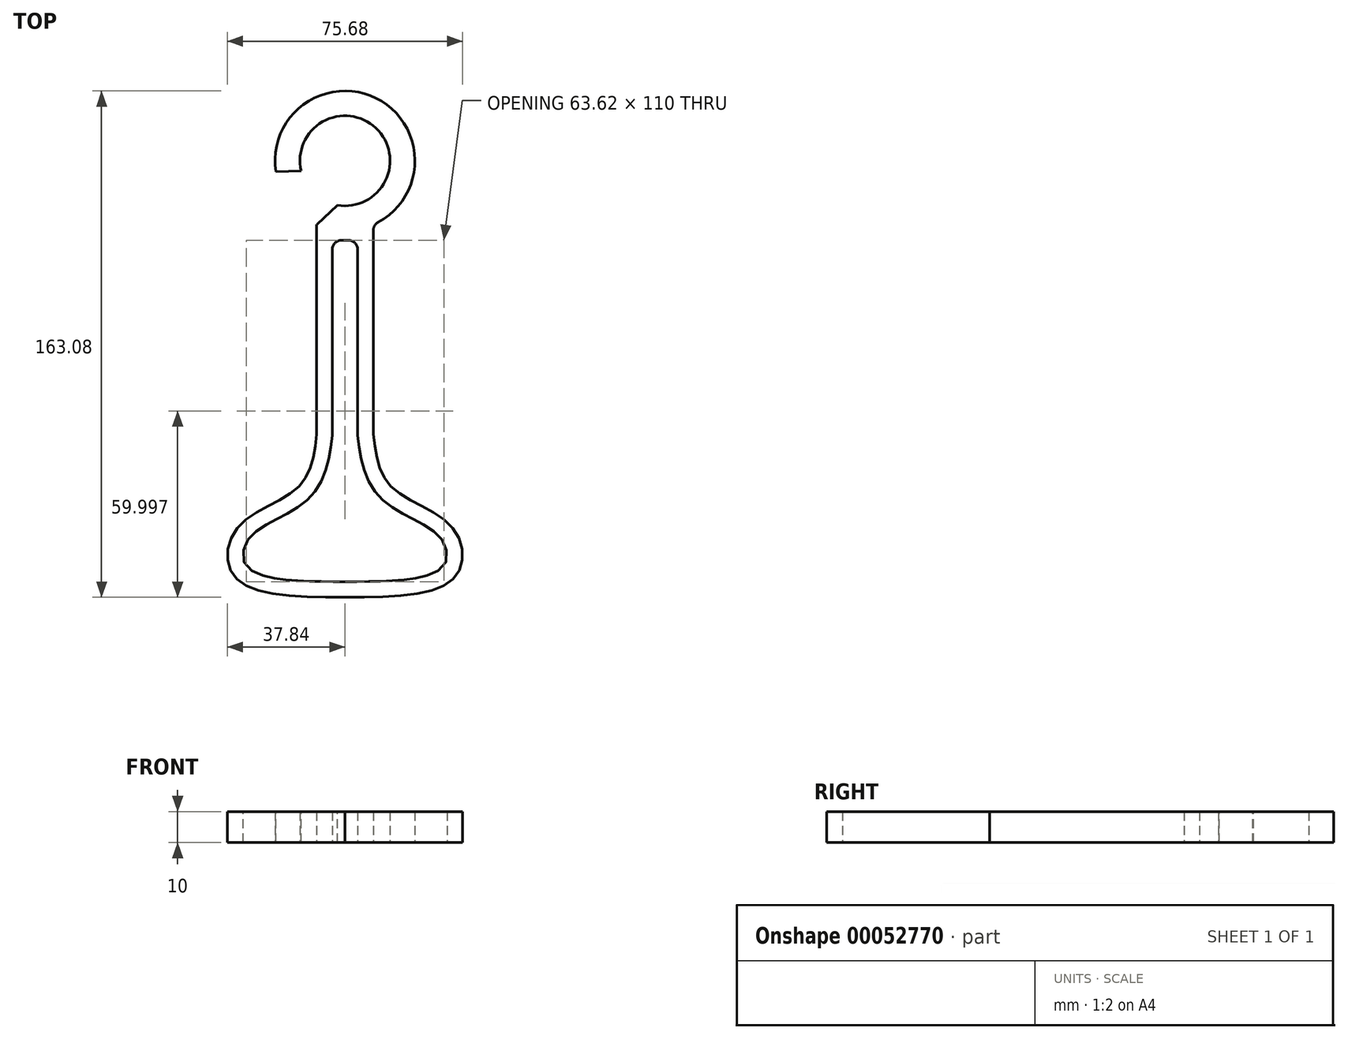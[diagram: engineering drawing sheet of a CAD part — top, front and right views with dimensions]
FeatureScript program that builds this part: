
annotation { "Feature Type Name" : "Feature", "Feature Type Description" : "" }
export const myFeature = defineFeature(function(context is Context, id is Id, definition is map)
    precondition{}
    {
        {
            var Q0;
            Q0=qCreatedBy(makeId("Top.planeOp"),FACE);
            var sketch = newSketch(context, id + "F0", { "sketchPlane" : qUnion([Q0])});
            skLineSegment(sketch, "E0", {"start": v(0, 67.57) * mm, "end": v(9.1, 67.57) * mm});
            skLineSegment(sketch, "E1", {"start": v(9.1, 67.57) * mm, "end": v(9.1, 0) * mm});
            skFitSpline(sketch, "E2", {"points": [v(9.1, 0) * mm, v(15.06, -16.95) * mm, v(34.56, -29.95) * mm, v(35.37, -45.93) * mm, v(0, -52.43) * mm], "startDerivative": vector(10.58, -85.23) * mm, "endDerivative": vector(-142.58, -0.73) * mm});
            skLineSegment(sketch, "E3", {"start": v(0, 67.57) * mm, "end": v(0, -52.43) * mm});
            skSolve(sketch);
        }
        {
            var Q0;
            Q0 = qSketchRegion(id + "F0", true);
            extrude(context, id + "F1", {"entities" : qUnion([Q0]), "depth" : 10 * mm});
        }
        {
            var Q0;
            Q0=makeQuery(id+"F1.opExtrude","SWEPT_BODY",BODY,{"disambiguationData":[OSD([sQuery(id+"F0.wireOp",EDGE,"E0"),sQuery(id+"F0.wireOp",EDGE,"E1"),sQuery(id+"F0.wireOp",EDGE,"E2"),sQuery(id+"F0.wireOp",EDGE,"E3")])]});
            var Q1;
            Q1=qCreatedBy(makeId("Right.planeOp"),FACE);
            mirror(context, id + "F2", {"operationType" : NewBodyOperationType.ADD, "entities" : qUnion([Q0]), "mirrorPlane" : qUnion([Q1])});
        }
        {
            var Q0;
            {var subQ0=makeQuery(id+"F1.opExtrude","CAP_FACE",FACE,{"disambiguationData":[OSD([sQuery(id+"F0.wireOp",EDGE,"E0"),sQuery(id+"F0.wireOp",EDGE,"E1"),sQuery(id+"F0.wireOp",EDGE,"E2"),sQuery(id+"F0.wireOp",EDGE,"E3")])],"isStart":false});Q0=makeQuery(id+"F2.boolean.opBoolean","MERGE",FACE,{"derivedFrom":[subQ0,makeQuery(id+"F2.opPattern","COPY",FACE,{"derivedFrom":subQ0,"instanceName":"1"})]});}
            var Q1;
            {var subQ0=makeQuery(id+"F1.opExtrude","CAP_FACE",FACE,{"disambiguationData":[OSD([sQuery(id+"F0.wireOp",EDGE,"E0"),sQuery(id+"F0.wireOp",EDGE,"E1"),sQuery(id+"F0.wireOp",EDGE,"E2"),sQuery(id+"F0.wireOp",EDGE,"E3")])],"isStart":true});Q1=makeQuery(id+"F2.boolean.opBoolean","MERGE",FACE,{"derivedFrom":[subQ0,makeQuery(id+"F2.opPattern","COPY",FACE,{"derivedFrom":subQ0,"instanceName":"1"})]});}
            shell(context, id + "F3", {"entities" : qUnion([Q0, Q1]), "thickness" : 5 * mm});
        }
        {
            var Q0;
            Q0=qCreatedBy(makeId("Top.planeOp"),FACE);
            var sketch = newSketch(context, id + "F4", { "sketchPlane" : qUnion([Q0])});
            skCircle(sketch, "E4", {"center": v(0, 88.15) * mm, "radius": 22.5 * mm});
            skSolve(sketch);
        }
        {
            var Q0;
            Q0=makeQuery(id+"F4.imprint","IMPRINT",FACE,{"disambiguationData":[TD([[makeQuery(id+"F4.imprint","IMPRINT",EDGE,{"derivedFrom":sQuery(id+"F4.wireOp",EDGE,"E4")}),1.0]])]});
            var Q1;
            {var subQ0=makeQuery(id+"F1.opExtrude","CAP_FACE",FACE,{"disambiguationData":[OSD([sQuery(id+"F0.wireOp",EDGE,"E0"),sQuery(id+"F0.wireOp",EDGE,"E1"),sQuery(id+"F0.wireOp",EDGE,"E2"),sQuery(id+"F0.wireOp",EDGE,"E3")])],"isStart":false});Q1=makeQuery(id+"F2.boolean.opBoolean","MERGE",FACE,{"derivedFrom":[subQ0,makeQuery(id+"F2.opPattern","COPY",FACE,{"derivedFrom":subQ0,"instanceName":"1"})]});}
            extrude(context, id + "F5", {"entities" : qUnion([Q0]), "endBound" : BoundingType.UP_TO_SURFACE, "endBoundEntityFace" : qUnion([Q1]), "depth" : 25 * mm});
        }
        {
            var Q0;
            Q0=makeQuery(id+"F5.opExtrude","CAP_FACE",FACE,{"disambiguationData":[OSD([sQuery(id+"F4.wireOp",EDGE,"E4")])],"isStart":false});
            var Q1;
            Q1=makeQuery(id+"F5.opExtrude","CAP_FACE",FACE,{"disambiguationData":[OSD([sQuery(id+"F4.wireOp",EDGE,"E4")])],"isStart":true});
            shell(context, id + "F6", {"entities" : qUnion([Q0, Q1]), "thickness" : 8 * mm});
        }
        {
            var Q0;
            Q0=makeQuery(id+"F5.opExtrude","CAP_FACE",FACE,{"disambiguationData":[OSD([sQuery(id+"F4.wireOp",EDGE,"E4")])],"isStart":false});
            var sketch = newSketch(context, id + "F7", { "sketchPlane" : qUnion([Q0])});
            skLineSegment(sketch, "E5", {"start": v(-22.23, 84.66) * mm, "end": v(-14.13, 84.9) * mm});
            skLineSegment(sketch, "E6", {"start": v(-14.13, 84.9) * mm, "end": v(-2.4, 73.85) * mm});
            skLineSegment(sketch, "E7", {"start": v(-2.4, 73.85) * mm, "end": v(-9.1, 67.57) * mm});
            skLineSegment(sketch, "E8", {"start": v(-9.1, 67.57) * mm, "end": v(-26.2, 68.97) * mm});
            skLineSegment(sketch, "E9", {"start": v(-26.2, 68.97) * mm, "end": v(-22.23, 84.66) * mm});
            skSolve(sketch);
        }
        {
            var Q0;
            Q0 = qSketchRegion(id + "F7", true);
            extrude(context, id + "F8", {"entities" : qUnion([Q0]), "operationType" : NewBodyOperationType.REMOVE, "endBound" : BoundingType.THROUGH_ALL, "oppositeDirection" : true, "depth" : 25 * mm});
        }
        {
            var Q0;
            Q0=makeQuery(id+"F1.opExtrude","SWEPT_BODY",BODY,{"disambiguationData":[OSD([sQuery(id+"F0.wireOp",EDGE,"E0"),sQuery(id+"F0.wireOp",EDGE,"E1"),sQuery(id+"F0.wireOp",EDGE,"E2"),sQuery(id+"F0.wireOp",EDGE,"E3")])]});
            var Q1;
            Q1=makeQuery(id+"F5.opExtrude","SWEPT_BODY",BODY,{"disambiguationData":[OSD([sQuery(id+"F4.wireOp",EDGE,"E4")])]});
            booleanBodies(context, id + "F9", {"operationType" : BooleanOperationType.UNION, "tools" : qUnion([Q0, Q1])});
        }
        {
            var Q0;
            Q0=makeQuery(id+"F8.boolean.opBoolean","COPY",EDGE,{"derivedFrom":makeQuery(id+"F8.opExtrude","SWEPT_EDGE",EDGE,{"disambiguationData":[OSD([sQuery(id+"F4.wireOp",EDGE,"E4"),sQuery(id+"F7.wireOp",EDGE,"E5"),sQuery(id+"F7.wireOp",EDGE,"E9")])]})});
            var Q1;
            Q1=makeQuery(id+"F8.boolean.opBoolean","COPY",EDGE,{"derivedFrom":makeQuery(id+"F8.opExtrude","SWEPT_EDGE",EDGE,{"disambiguationData":[OSD([sQuery(id+"F4.wireOp",EDGE,"E4"),sQuery(id+"F7.wireOp",EDGE,"E5"),sQuery(id+"F7.wireOp",EDGE,"E6")])]})});
            var Q2;
            Q2=makeQuery(id+"F8.boolean.opBoolean","COPY",EDGE,{"derivedFrom":makeQuery(id+"F8.opExtrude","SWEPT_EDGE",EDGE,{"disambiguationData":[OSD([sQuery(id+"F4.wireOp",EDGE,"E4"),sQuery(id+"F7.wireOp",EDGE,"E6"),sQuery(id+"F7.wireOp",EDGE,"E7")])]})});
            var Q3;
            {var subQ0=sQuery(id+"F0.wireOp",EDGE,"E1");var subQ1=sQuery(id+"F0.wireOp",EDGE,"E0");Q3=makeQuery(id+"F3.opShell","OFFSET_EDGE",EDGE,{"disambiguationData":[OSD([subQ1,subQ0]),TDD([makeQuery(id+"F2.opPattern","COPY",EDGE,{"derivedFrom":makeQuery(id+"F1.opExtrude","SWEPT_EDGE",EDGE,{"disambiguationData":[OSD([subQ1,subQ0])]}),"instanceName":"1"})])]});}
            var Q4;
            {var subQ0=sQuery(id+"F0.wireOp",EDGE,"E1");var subQ1=sQuery(id+"F0.wireOp",EDGE,"E0");Q4=makeQuery(id+"F3.opShell","OFFSET_EDGE",EDGE,{"disambiguationData":[OSD([subQ1,subQ0]),TDD([makeQuery(id+"F1.opExtrude","SWEPT_EDGE",EDGE,{"disambiguationData":[OSD([subQ1,subQ0])]})])]});}
            var Q5;
            Q5=makeQuery(id+"F9.opBoolean","INTERSECT",EDGE,{"derivedFrom":[makeQuery(id+"F1.opExtrude","SWEPT_FACE",FACE,{"disambiguationData":[OSD([sQuery(id+"F0.wireOp",EDGE,"E1")])]}),makeQuery(id+"F5.opExtrude","SWEPT_FACE",FACE,{"disambiguationData":[OSD([sQuery(id+"F4.wireOp",EDGE,"E4")])]})]});
            var Q6;
            Q6=makeQuery(id+"F8.boolean.opBoolean","COPY",EDGE,{"derivedFrom":makeQuery(id+"F8.opExtrude","SWEPT_EDGE",EDGE,{"disambiguationData":[OSD([sQuery(id+"F4.wireOp",EDGE,"E4"),sQuery(id+"F7.wireOp",EDGE,"E7"),sQuery(id+"F7.wireOp",EDGE,"E8")])]})});
            var Q7;
            {var subQ0=makeQuery(id+"F1.opExtrude","SWEPT_FACE",FACE,{"disambiguationData":[OSD([sQuery(id+"F0.wireOp",EDGE,"E0")])]});Q7=makeQuery(id+"F9.opBoolean","INTERSECT",EDGE,{"derivedFrom":[makeQuery(id+"F2.boolean.opBoolean","MERGE",FACE,{"derivedFrom":[subQ0,makeQuery(id+"F2.opPattern","COPY",FACE,{"derivedFrom":subQ0,"instanceName":"1"})]}),makeQuery(id+"F8.boolean.opBoolean","COPY",FACE,{"derivedFrom":makeQuery(id+"F8.opExtrude","SWEPT_FACE",FACE,{"disambiguationData":[OSD([sQuery(id+"F7.wireOp",EDGE,"E7")])]})})]});}
            fillet(context, id + "F10", {"entities" : qUnion([Q0, Q1, Q2, Q3, Q4, Q5, Q6, Q7]), "radius" : 3 * mm, "tangentPropagation" : true, "allowEdgeOverflow" : false});
        }
    });
